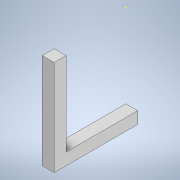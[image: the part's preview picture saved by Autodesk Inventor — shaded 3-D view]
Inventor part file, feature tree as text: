
AUTODESK INVENTOR PART (.ipt)
format: ipt  version: 2020 (Build 240168000, 168)  size: 103,936 bytes
history: native  units: in
note: dims shown in document units (in); Inventor stores cm internally (conversion verified against a paired STEP export)
features: sketch x3, extrude x2
ambient origin geometry x8: Origin, YZ Plane, XZ Plane, XY Plane, X Axis, Y Axis, Z Axis, Center Point
bodies: Solid1 (feature_tree)
feature tree (5):
  extrude  "Extrusion1"  Depth=0.7874in
  extrude  "Extrusion2"  Depth=0.7874in
  sketch  "Sketch3"  dims[d5=5.5118in d6=0.0in]
  sketch  "Sketch1"  dims[d0=0.7874in d1=0.7874in]
  sketch  "Sketch2"  dims[d2=5.5118in d3=0.0in d4=0.7874in]
